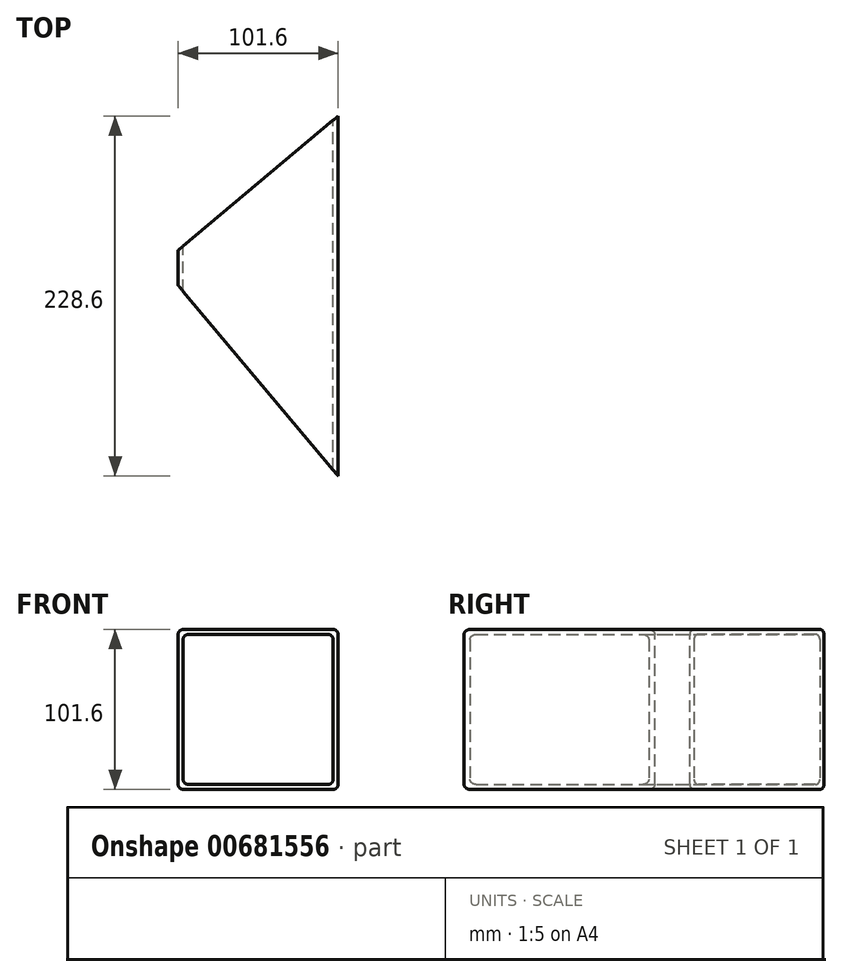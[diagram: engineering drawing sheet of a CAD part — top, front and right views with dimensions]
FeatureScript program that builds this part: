
annotation { "Feature Type Name" : "Feature", "Feature Type Description" : "" }
export const myFeature = defineFeature(function(context is Context, id is Id, definition is map)
    precondition{}
    {
        {
            var Q0;
            Q0=qCreatedBy(makeId("Front.planeOp"),FACE);
            var sketch = newSketch(context, id + "F0", { "sketchPlane" : qUnion([Q0])});
            skLineSegment(sketch, "E0.bottom", {"start": v(47.63, 50.8) * mm, "end": v(-47.63, 50.8) * mm});
            skLineSegment(sketch, "E0.top", {"start": v(47.63, -50.8) * mm, "end": v(-47.63, -50.8) * mm});
            skLineSegment(sketch, "E0.left", {"start": v(50.8, 47.62) * mm, "end": v(50.8, -47.62) * mm});
            skLineSegment(sketch, "E0.right", {"start": v(-50.8, 47.62) * mm, "end": v(-50.8, -47.63) * mm});
            skPoint(sketch, "E0.middle", {"position": v(0, 0) * mm});
            skLineSegment(sketch, "E1.0", {"start": v(44.45, 47.62) * mm, "end": v(-44.45, 47.62) * mm});
            skLineSegment(sketch, "E1.1", {"start": v(47.63, 44.45) * mm, "end": v(47.63, -44.45) * mm});
            skLineSegment(sketch, "E1.2", {"start": v(44.45, -47.62) * mm, "end": v(-44.45, -47.62) * mm});
            skLineSegment(sketch, "E1.3", {"start": v(-47.63, 44.45) * mm, "end": v(-47.63, -44.45) * mm});
            skPoint(sketch, "E2.visualSharp", {"position": v(-47.63, 47.62) * mm});
            skArc(sketch, "E2.filletArc", {"start": v(-44.45, 47.62) * mm, "mid": v(-46.7, 46.7) * mm, "end": v(-47.63, 44.45) * mm});
            skPoint(sketch, "E3.visualSharp", {"position": v(-50.8, 50.8) * mm});
            skArc(sketch, "E3.filletArc", {"start": v(-47.63, 50.8) * mm, "mid": v(-49.87, 49.87) * mm, "end": v(-50.8, 47.62) * mm});
            skPoint(sketch, "E4.visualSharp", {"position": v(47.63, 47.62) * mm});
            skArc(sketch, "E4.filletArc", {"start": v(47.63, 44.45) * mm, "mid": v(46.7, 46.7) * mm, "end": v(44.45, 47.62) * mm});
            skPoint(sketch, "E5.visualSharp", {"position": v(50.8, 50.8) * mm});
            skArc(sketch, "E5.filletArc", {"start": v(50.8, 47.62) * mm, "mid": v(49.87, 49.87) * mm, "end": v(47.63, 50.8) * mm});
            skPoint(sketch, "E6.visualSharp", {"position": v(-47.63, -47.62) * mm});
            skArc(sketch, "E6.filletArc", {"start": v(-47.63, -44.45) * mm, "mid": v(-46.7, -46.7) * mm, "end": v(-44.45, -47.62) * mm});
            skPoint(sketch, "E7.visualSharp", {"position": v(-50.8, -50.8) * mm});
            skArc(sketch, "E7.filletArc", {"start": v(-50.8, -47.63) * mm, "mid": v(-49.87, -49.87) * mm, "end": v(-47.63, -50.8) * mm});
            skPoint(sketch, "E8.visualSharp", {"position": v(47.63, -47.62) * mm});
            skArc(sketch, "E8.filletArc", {"start": v(44.45, -47.62) * mm, "mid": v(46.7, -46.7) * mm, "end": v(47.63, -44.45) * mm});
            skPoint(sketch, "E9.visualSharp", {"position": v(50.8, -50.8) * mm});
            skArc(sketch, "E9.filletArc", {"start": v(47.63, -50.8) * mm, "mid": v(49.87, -49.87) * mm, "end": v(50.8, -47.62) * mm});
            skSolve(sketch);
        }
        {
            var Q0;
            Q0=qSketchRegion(id+"F0",true);
            extrude(context, id + "F1", {"entities" : qUnion([Q0]), "depth" : 228.6 * mm, "offsetDistance" : 25.4 * mm});
        }
        {
            var Q0;
            Q0=qCreatedBy(makeId("Top.planeOp"),FACE);
            var sketch = newSketch(context, id + "F2", { "sketchPlane" : qUnion([Q0])});
            skLineSegment(sketch, "E10.bottom", {"start": v(-50.8, 0) * mm, "end": v(50.8, 0) * mm});
            skLineSegment(sketch, "E10.left", {"start": v(-50.8, -85.25) * mm, "end": v(-50.8, 0) * mm});
            skLineSegment(sketch, "E11.bottom", {"start": v(-50.8, -228.6) * mm, "end": v(50.8, -228.6) * mm});
            skLineSegment(sketch, "E11.left", {"start": v(-50.8, -228.6) * mm, "end": v(-50.8, -107.52) * mm});
            skLineSegment(sketch, "E11.right", {"start": v(50.8, -228.6) * mm, "end": v(50.8, -107.52) * mm});
            skLineSegment(sketch, "E12", {"start": v(-50.8, -107.52) * mm, "end": v(50.8, -228.6) * mm});
            skLineSegment(sketch, "E13", {"start": v(-50.8, -85.25) * mm, "end": v(50.8, 0) * mm});
            skSolve(sketch);
        }
        {
            var Q0;
            Q0 = qSketchRegion(id + "F2", true);
            extrude(context, id + "F3", {"entities" : qUnion([Q0]), "operationType" : NewBodyOperationType.REMOVE, "endBound" : BoundingType.THROUGH_ALL, "oppositeDirection" : true, "depth" : 25.4 * mm, "offsetDistance" : 25.4 * mm, "hasSecondDirection" : true, "secondDirectionBound" : SecondDirectionBoundingType.THROUGH_ALL, "secondDirectionOppositeDirection" : false, "secondDirectionDepth" : 25.4 * mm});
        }
    });
